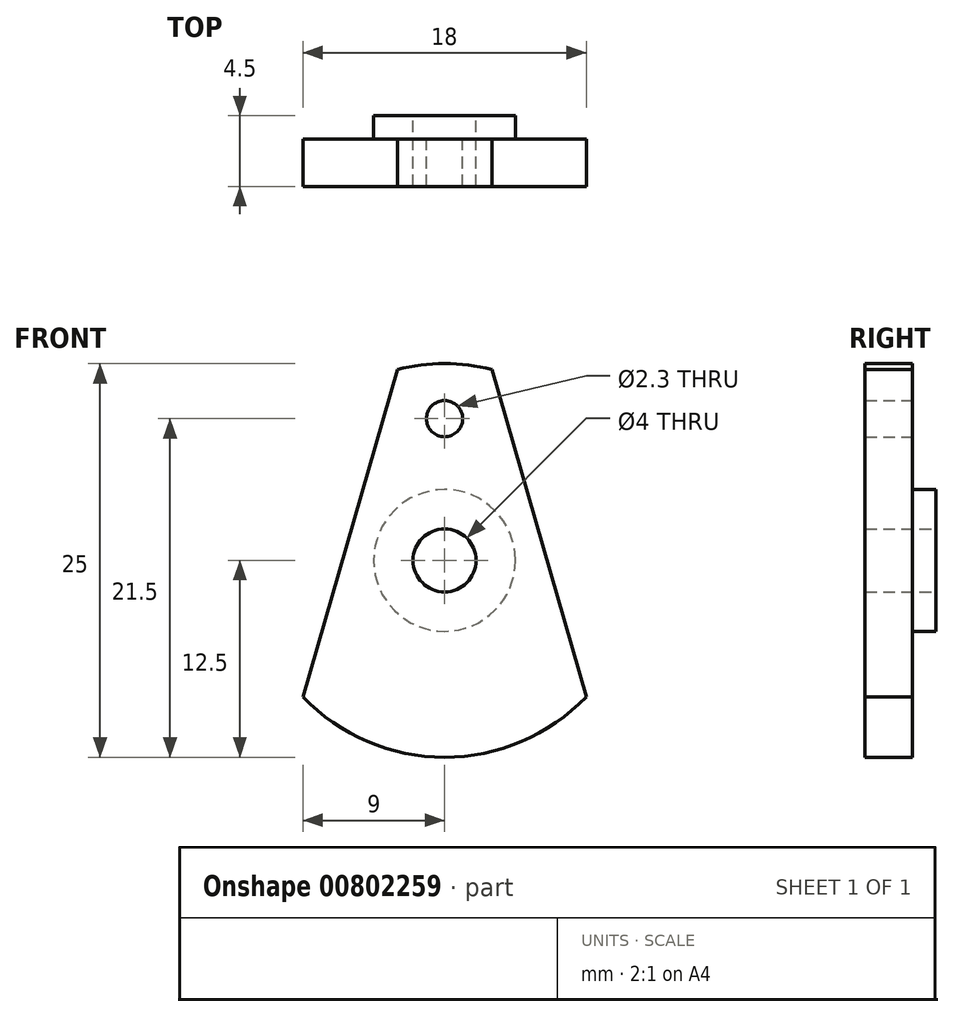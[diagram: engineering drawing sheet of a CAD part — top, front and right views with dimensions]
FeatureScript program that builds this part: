
annotation { "Feature Type Name" : "Feature", "Feature Type Description" : "" }
export const myFeature = defineFeature(function(context is Context, id is Id, definition is map)
    precondition{}
    {
        {
            var Q0;
            Q0=qCreatedBy(makeId("Front.planeOp"),FACE);
            var sketch = newSketch(context, id + "F0", { "sketchPlane" : qUnion([Q0])});
            skArc(sketch, "E0", {"start": v(3, 12.13) * mm, "mid": v(0, 12.5) * mm, "end": v(-3, 12.13) * mm});
            skLineSegment(sketch, "E1", {"start": v(3, 12.13) * mm, "end": v(9, -8.67) * mm});
            skLineSegment(sketch, "E2.MirrorCS", {"start": v(-3, 12.13) * mm, "end": v(-9, -8.67) * mm});
            skPoint(sketch, "E3.orphan", {"position": v(9, -33.49) * mm});
            skPoint(sketch, "E4.orphan", {"position": v(3, -33.49) * mm});
            skArc(sketch, "E5.trimOffspring", {"start": v(-9, -8.67) * mm, "mid": v(0, -12.5) * mm, "end": v(9, -8.67) * mm});
            skCircle(sketch, "E6", {"center": v(0, 0) * mm, "radius": 4.5 * mm});
            skCircle(sketch, "E7", {"center": v(0, 0) * mm, "radius": 2 * mm});
            skCircle(sketch, "E8", {"center": v(0, 9) * mm, "radius": 1.15 * mm});
            skSolve(sketch);
        }
        {
            var Q0;
            Q0 = qSketchRegion(id + "F0", true);
            var Q1;
            Q1=makeQuery(id+"F0.imprint","IMPRINT",FACE,{"disambiguationData":[TD([[makeQuery(id+"F0.imprint","IMPRINT",EDGE,{"derivedFrom":sQuery(id+"F0.wireOp",EDGE,"E6")}),1.0]])]});
            extrude(context, id + "F1", {"entities" : qUnion([Q0, Q1]), "depth" : 3 * mm, "offsetDistance" : 25 * mm});
        }
        {
            var Q0;
            Q0=makeQuery(id+"F0.imprint","IMPRINT",FACE,{"disambiguationData":[TD([[makeQuery(id+"F0.imprint","IMPRINT",EDGE,{"derivedFrom":sQuery(id+"F0.wireOp",EDGE,"E6")}),1.0]])]});
            extrude(context, id + "F2", {"entities" : qUnion([Q0]), "operationType" : NewBodyOperationType.ADD, "oppositeDirection" : true, "depth" : 1.5 * mm, "offsetDistance" : 25 * mm});
        }
    });
